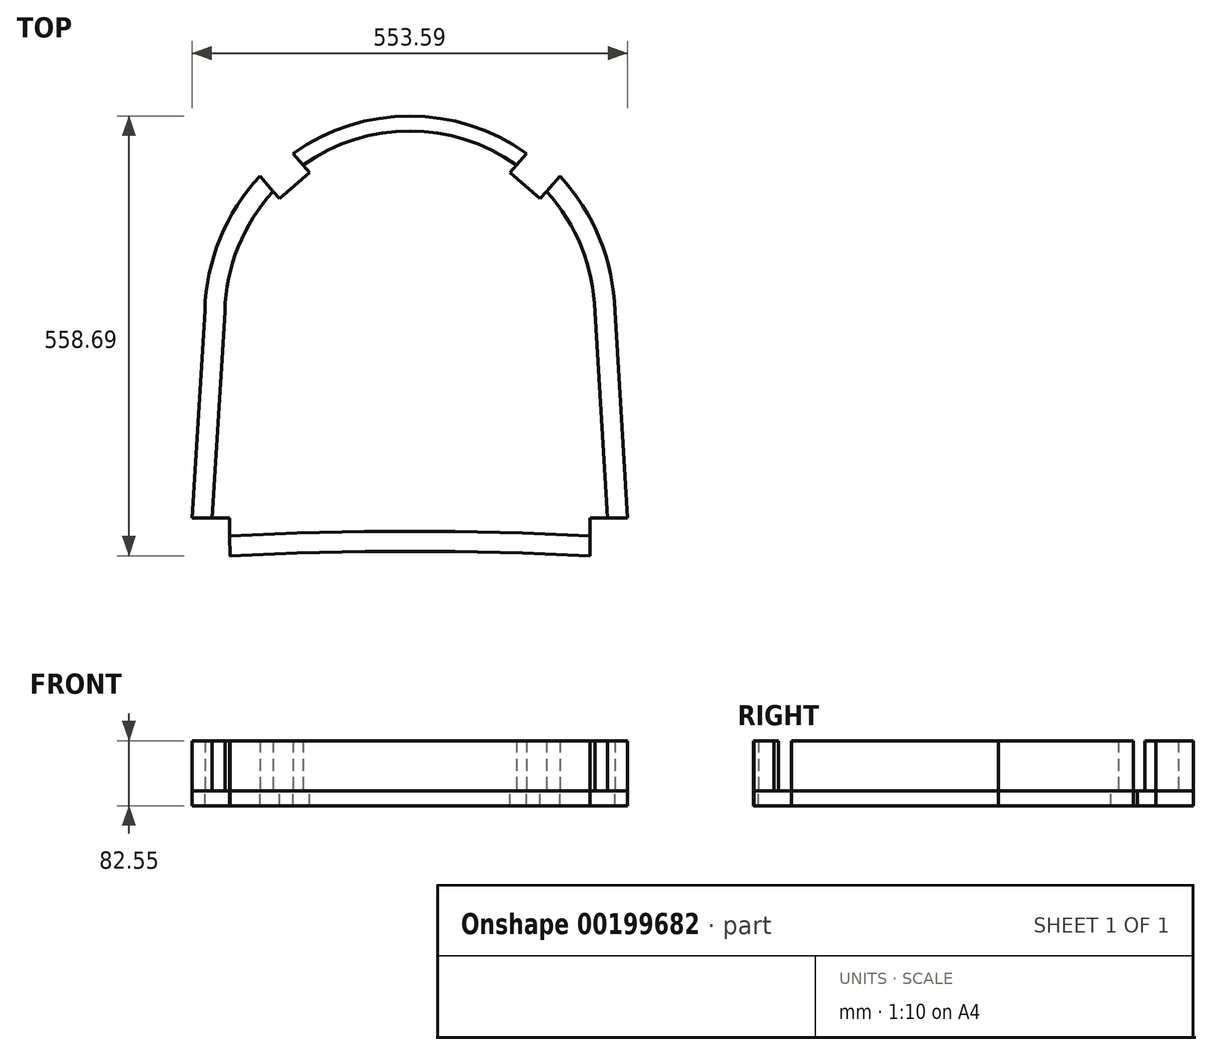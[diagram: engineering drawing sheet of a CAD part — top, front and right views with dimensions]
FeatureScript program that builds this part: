
annotation { "Feature Type Name" : "Feature", "Feature Type Description" : "" }
export const myFeature = defineFeature(function(context is Context, id is Id, definition is map)
    precondition{}
    {
        {
            var Q0;
            Q0=qCreatedBy(makeId("Top.planeOp"),FACE);
            var sketch = newSketch(context, id + "F0", { "sketchPlane" : qUnion([Q0])});
            skLineSegment(sketch, "E0", {"start": v(-279.4, 0) * mm, "end": v(-279.4, 8.66) * mm, "construction": true});
            skLineSegment(sketch, "E1", {"start": v(-101.6, 0) * mm, "end": v(-101.6, 5.16) * mm, "construction": true});
            skLineSegment(sketch, "E2", {"start": v(-457.2, 0) * mm, "end": v(-457.2, 5.16) * mm, "construction": true});
            skLineSegment(sketch, "E3", {"start": v(-558.8, 304.8) * mm, "end": v(-539.75, 304.8) * mm, "construction": true});
            skArc(sketch, "E4", {"start": v(-19.05, 304.8) * mm, "mid": v(-38.28, 396.78) * mm, "end": v(-88.9, 475.94) * mm});
            skLineSegment(sketch, "E5", {"start": v(-539.75, 305.45) * mm, "end": v(-539.75, 304.8) * mm, "construction": true});
            skLineSegment(sketch, "E6", {"start": v(-19.05, 0) * mm, "end": v(-19.05, 1.14) * mm, "construction": true});
            skLineSegment(sketch, "E7", {"start": v(-556.2, 41.69) * mm, "end": v(-539.75, 305.45) * mm});
            skLineSegment(sketch, "E8", {"start": v(-2.6, 41.73) * mm, "end": v(-19.05, 304.8) * mm});
            skPoint(sketch, "E9.orphan", {"position": v(-101.6, 558.8) * mm});
            skPoint(sketch, "E10.orphan", {"position": v(-279.4, 558.8) * mm});
            skLineSegment(sketch, "E11.trimOffspring", {"start": v(-539.75, 1.14) * mm, "end": v(-539.75, 0) * mm, "construction": true});
            skPoint(sketch, "E12.orphan", {"position": v(-558.8, 558.8) * mm});
            skLineSegment(sketch, "E13.trimOffspring", {"start": v(-279.4, 558.8) * mm, "end": v(-279.4, 558.8) * mm, "construction": true});
            skPoint(sketch, "E14.top.start.orphan", {"position": v(0, 558.8) * mm});
            skLineSegment(sketch, "E15.top", {"start": v(-556.2, 41.69) * mm, "end": v(-508.57, 41.69) * mm});
            skLineSegment(sketch, "E15.right", {"start": v(-508, -6.24) * mm, "end": v(-508.57, 41.69) * mm});
            skLineSegment(sketch, "E16.top", {"start": v(-2.6, 41.73) * mm, "end": v(-50.23, 41.73) * mm});
            skLineSegment(sketch, "E16.right", {"start": v(-50.8, -6.2) * mm, "end": v(-50.23, 41.73) * mm});
            skPoint(sketch, "E17", {"position": v(-556.2, 41.69) * mm});
            skPoint(sketch, "E18", {"position": v(-508, -6.24) * mm});
            skPoint(sketch, "E19", {"position": v(-2.6, 41.73) * mm});
            skPoint(sketch, "E20", {"position": v(-50.8, -6.2) * mm});
            skArc(sketch, "E21.trimOffspring", {"start": v(-50.8, -6.2) * mm, "mid": v(-279.4, -0.42) * mm, "end": v(-508, -6.24) * mm});
            skPoint(sketch, "E16.bottom.start.orphan", {"position": v(0, 0) * mm});
            skPoint(sketch, "E22.trimOffspring.end.orphan", {"position": v(-558.8, 0) * mm});
            skLineSegment(sketch, "E23", {"start": v(-279.4, 558.8) * mm, "end": v(-279.4, 471.65) * mm, "construction": true});
            skPoint(sketch, "E24", {"position": v(-431.8, 509.55) * mm});
            skLineSegment(sketch, "E25", {"start": v(-469.9, 475.95) * mm, "end": v(-444.7, 447.37) * mm});
            skLineSegment(sketch, "E26", {"start": v(-444.7, 447.37) * mm, "end": v(-406.6, 480.98) * mm});
            skLineSegment(sketch, "E27", {"start": v(-406.6, 480.98) * mm, "end": v(-431.8, 509.55) * mm});
            skArc(sketch, "E28.trimOffspring", {"start": v(-469.9, 475.95) * mm, "mid": v(-520.4, 397.08) * mm, "end": v(-539.75, 305.45) * mm});
            skLineSegment(sketch, "E29.MirrorCS", {"start": v(-152.2, 480.98) * mm, "end": v(-127, 509.55) * mm});
            skLineSegment(sketch, "E30.MirrorCS", {"start": v(-114.1, 447.37) * mm, "end": v(-152.2, 480.98) * mm});
            skLineSegment(sketch, "E31.MirrorCS", {"start": v(-88.9, 475.95) * mm, "end": v(-114.1, 447.37) * mm});
            skArc(sketch, "E32.trimOffspring", {"start": v(-127, 509.55) * mm, "mid": v(-279.4, 558.8) * mm, "end": v(-431.8, 509.55) * mm});
            skArc(sketch, "E33.0", {"start": v(-50.5, 19.21) * mm, "mid": v(-279.4, 24.98) * mm, "end": v(-508.3, 19.18) * mm});
            skArc(sketch, "E34.0", {"start": v(-44.43, 303.7) * mm, "mid": v(-61.24, 385.8) * mm, "end": v(-105.79, 456.8) * mm});
            skLineSegment(sketch, "E34.1", {"start": v(-28.06, 41.73) * mm, "end": v(-44.43, 303.7) * mm});
            skArc(sketch, "E35.0", {"start": v(-143.89, 490.4) * mm, "mid": v(-279.4, 533.4) * mm, "end": v(-414.92, 490.4) * mm});
            skLineSegment(sketch, "E36.0", {"start": v(-530.75, 41.69) * mm, "end": v(-514.37, 304.33) * mm});
            skArc(sketch, "E36.1", {"start": v(-453.02, 456.8) * mm, "mid": v(-497.45, 386.1) * mm, "end": v(-514.37, 304.33) * mm});
            skArc(sketch, "E37.0", {"start": v(-131.22, 504.76) * mm, "mid": v(-279.4, 552.45) * mm, "end": v(-427.59, 504.77) * mm});
            skArc(sketch, "E38.0", {"start": v(-465.69, 471.16) * mm, "mid": v(-514.67, 394.34) * mm, "end": v(-533.4, 305.17) * mm});
            skLineSegment(sketch, "E38.1", {"start": v(-549.3, 50.4) * mm, "end": v(-533.4, 305.17) * mm});
            skArc(sketch, "E39.0", {"start": v(-25.4, 304.52) * mm, "mid": v(-44.02, 394.03) * mm, "end": v(-93.12, 471.16) * mm});
            skLineSegment(sketch, "E39.1", {"start": v(-9.51, 50.4) * mm, "end": v(-25.4, 304.52) * mm});
            skArc(sketch, "E40.0", {"start": v(-50.1, 0.12) * mm, "mid": v(-279.02, 5.93) * mm, "end": v(-507.94, 0.12) * mm});
            skSolve(sketch);
        }
        {
            var Q0;
            {var subQ0=sQuery(id+"F0.wireOp",EDGE,"E33.0");Q0=makeQuery(id+"F0.imprint","IMPRINT",FACE,{"disambiguationData":[TD([[makeQuery(id+"F0.imprint","IMPRINT",EDGE,{"derivedFrom":subQ0}),1.0]])]});}
            var Q1;
            {var subQ6=sQuery(id+"F0.wireOp",EDGE,"E34.0");Q1=makeQuery(id+"F0.imprint","IMPRINT",FACE,{"disambiguationData":[TD([[makeQuery(id+"F0.imprint","IMPRINT",EDGE,{"derivedFrom":subQ6}),-1.0]])]});}
            var Q2;
            {var subQ0=sQuery(id+"F0.wireOp",EDGE,"E35.0");Q2=makeQuery(id+"F0.imprint","IMPRINT",FACE,{"disambiguationData":[TD([[makeQuery(id+"F0.imprint","IMPRINT",EDGE,{"derivedFrom":subQ0}),-1.0]])]});}
            var Q3;
            {var subQ0=sQuery(id+"F0.wireOp",EDGE,"E36.0");Q3=makeQuery(id+"F0.imprint","IMPRINT",FACE,{"disambiguationData":[TD([[makeQuery(id+"F0.imprint","IMPRINT",EDGE,{"derivedFrom":subQ0}),1.0]])]});}
            extrude(context, id + "F1", {"entities" : qUnion([Q0, Q1, Q2, Q3]), "depth" : 63.5 * mm});
        }
        {
            var Q0;
            Q0 = qSketchRegion(id + "F0", true);
            extrude(context, id + "F2", {"entities" : qUnion([Q0]), "oppositeDirection" : true, "depth" : 19.05 * mm});
        }
    });
